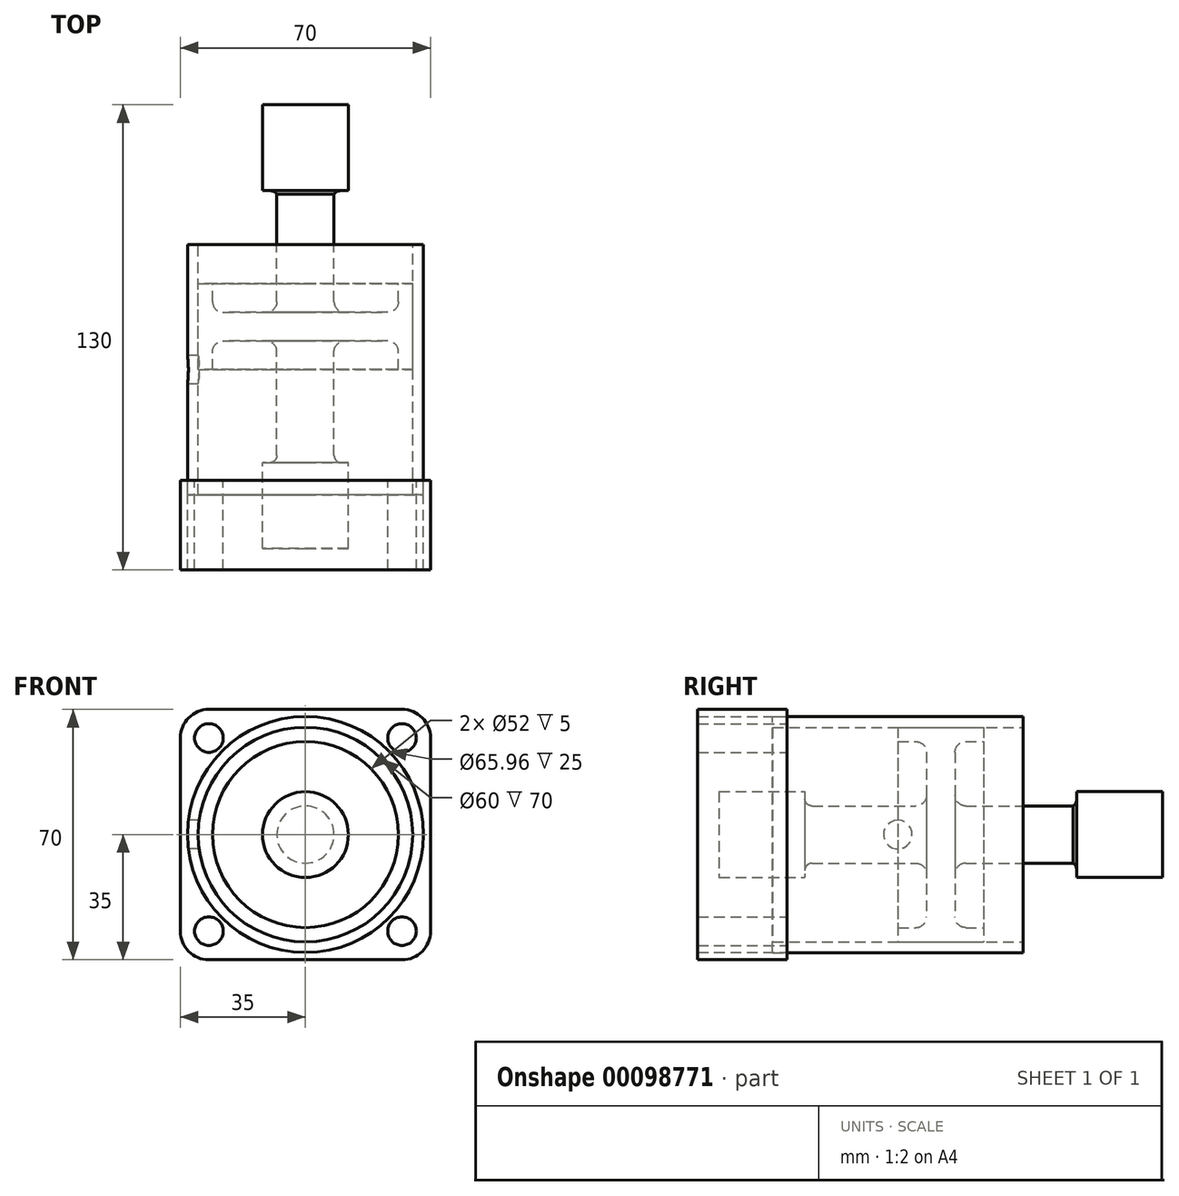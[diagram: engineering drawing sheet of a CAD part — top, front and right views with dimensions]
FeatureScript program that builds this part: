
annotation { "Feature Type Name" : "Feature", "Feature Type Description" : "" }
export const myFeature = defineFeature(function(context is Context, id is Id, definition is map)
    precondition{}
    {
        {
            var Q0;
            Q0=qCreatedBy(makeId("Right.planeOp"),FACE);
            var sketch = newSketch(context, id + "F0", { "sketchPlane" : qUnion([Q0])});
            skLineSegment(sketch, "E0", {"start": v(0, 26) * mm, "end": v(0, 30) * mm});
            skLineSegment(sketch, "E1", {"start": v(0, 30) * mm, "end": v(24, 30) * mm});
            skLineSegment(sketch, "E2", {"start": v(24, 30) * mm, "end": v(24, 26) * mm});
            skLineSegment(sketch, "E3", {"start": v(50, 9.73) * mm, "end": v(50, 12) * mm});
            skLineSegment(sketch, "E4", {"start": v(50, 12) * mm, "end": v(74, 12) * mm});
            skLineSegment(sketch, "E5", {"start": v(74, 12) * mm, "end": v(74, 0) * mm});
            skLineSegment(sketch, "E6", {"start": v(74, 0) * mm, "end": v(-50, 0) * mm});
            skLineSegment(sketch, "E7", {"start": v(-50, 0) * mm, "end": v(-50, 12) * mm});
            skLineSegment(sketch, "E8", {"start": v(-50, 12) * mm, "end": v(-26, 12) * mm});
            skLineSegment(sketch, "E9", {"start": v(-26, 12) * mm, "end": v(-26, 10) * mm});
            skPoint(sketch, "E10.visualSharp", {"position": v(-26, 8) * mm});
            skArc(sketch, "E10.filletArc", {"start": v(-26, 10) * mm, "mid": v(-25.41, 8.59) * mm, "end": v(-24, 8) * mm});
            skPoint(sketch, "E11.visualSharp", {"position": v(0, 8) * mm});
            skPoint(sketch, "E12.visualSharp", {"position": v(24, 8) * mm});
            skPoint(sketch, "E13.visualSharp", {"position": v(50, 8) * mm});
            skArc(sketch, "E13.filletArc", {"start": v(49, 8) * mm, "mid": v(49.73, 8.73) * mm, "end": v(50, 9.73) * mm});
            skLineSegment(sketch, "E14", {"start": v(-24, 8) * mm, "end": v(5, 8) * mm});
            skLineSegment(sketch, "E15", {"start": v(0, 26) * mm, "end": v(5, 26) * mm});
            skLineSegment(sketch, "E16", {"start": v(8, 23) * mm, "end": v(8, 11) * mm});
            skLineSegment(sketch, "E17", {"start": v(24, 26) * mm, "end": v(19, 26) * mm});
            skLineSegment(sketch, "E18", {"start": v(16, 23) * mm, "end": v(16, 11) * mm});
            skLineSegment(sketch, "E19.trimOffspring", {"start": v(19, 8) * mm, "end": v(49, 8) * mm});
            skPoint(sketch, "E20.visualSharp", {"position": v(8, 26) * mm});
            skArc(sketch, "E20.filletArc", {"start": v(8, 23) * mm, "mid": v(7.12, 25.12) * mm, "end": v(5, 26) * mm});
            skPoint(sketch, "E21.visualSharp", {"position": v(16, 26) * mm});
            skArc(sketch, "E21.filletArc", {"start": v(19, 26) * mm, "mid": v(16.88, 25.12) * mm, "end": v(16, 23) * mm});
            skPoint(sketch, "E22.visualSharp", {"position": v(8, 8) * mm});
            skArc(sketch, "E22.filletArc", {"start": v(5, 8) * mm, "mid": v(7.12, 8.88) * mm, "end": v(8, 11) * mm});
            skPoint(sketch, "E23.visualSharp", {"position": v(16, 8) * mm});
            skArc(sketch, "E23.filletArc", {"start": v(16, 11) * mm, "mid": v(16.88, 8.88) * mm, "end": v(19, 8) * mm});
            skSolve(sketch);
        }
        {
            var Q0;
            Q0=makeQuery(id+"F0.imprint","IMPRINT",FACE,{"disambiguationData":[TD([[makeQuery(id+"F0.imprint","IMPRINT",EDGE,{"derivedFrom":sQuery(id+"F0.wireOp",EDGE,"E0")}),-1.0]])]});
            var Q1;
            Q1=sQuery(id+"F0.wireOp",EDGE,"E6");
            revolve(context, id + "F1", {"surfaceOperationType" : NewSurfaceOperationType.NEW, "entities" : qUnion([Q0]), "axis" : qUnion([Q1]), "revolveType" : RevolveType.FULL});
        }
        {
            var Q0;
            Q0=makeQuery(id+"F1.opRevolve","SWEPT_FACE",FACE,{"disambiguationData":[OSD([sQuery(id+"F0.wireOp",EDGE,"E0")])]});
            var sketch = newSketch(context, id + "F2", { "sketchPlane" : qUnion([Q0])});
            skCircle(sketch, "E24", {"center": v(0, 0) * mm, "radius": 30 * mm});
            skCircle(sketch, "E25", {"center": v(0, 0) * mm, "radius": 33 * mm});
            skSolve(sketch);
        }
        {
            var Q0;
            Q0=makeQuery(id+"F2.imprint","IMPRINT",FACE,{"disambiguationData":[TD([[makeQuery(id+"F2.imprint","IMPRINT",EDGE,{"derivedFrom":sQuery(id+"F2.wireOp",EDGE,"E24")}),1.0]])]});
            extrude(context, id + "F3", {"entities" : qUnion([Q0]), "depth" : 70 * mm, "symmetric" : true});
        }
        {
            var Q0;
            Q0=qCreatedBy(makeId("Right.planeOp"),FACE);
            var sketch = newSketch(context, id + "F4", { "sketchPlane" : qUnion([Q0])});
            skPoint(sketch, "E26", {"position": v(0, 0) * mm});
            skSolve(sketch);
        }
        {
            var Q0;
            Q0=sQuery(id+"F4.wireOp",VERTEX,"E26");
            var Q1;
            Q1=makeQuery(id+"F3.opExtrude","SWEPT_BODY",BODY,{"disambiguationData":[OSD([sQuery(id+"F2.wireOp",EDGE,"E24"),sQuery(id+"F2.wireOp",EDGE,"E25")])]});
            hole(context, id + "F5", {"style" : HoleStyle.SIMPLE, "endStyle" : HoleEndStyle.BLIND, "holeDiameter" : 8 * mm, "holeDepth" : 70 * mm, "locations" : qUnion([Q0]), "scope" : qUnion([Q1])});
        }
        {
            var Q0;
            Q0=makeQuery(id+"F3.opExtrude","CAP_FACE",FACE,{"disambiguationData":[OSD([sQuery(id+"F2.wireOp",EDGE,"E24"),sQuery(id+"F2.wireOp",EDGE,"E25")])],"isStart":false});
            cPlane(context, id + "F6", {"entities" : qUnion([Q0]), "cplaneType" : CPlaneType.OFFSET, "offset" : 4 * mm, "oppositeDirection" : true, "width" : 150 * mm, "height" : 150 * mm});
        }
        {
            var Q0;
            Q0=qCreatedBy(id+"F6.planeOp",FACE);
            var sketch = newSketch(context, id + "F7", { "sketchPlane" : qUnion([Q0])});
            skLineSegment(sketch, "E27.bottom", {"start": v(27, 35) * mm, "end": v(-27, 35) * mm});
            skLineSegment(sketch, "E27.top", {"start": v(27, -35) * mm, "end": v(-27, -35) * mm});
            skLineSegment(sketch, "E27.left", {"start": v(35, 27) * mm, "end": v(35, -27) * mm});
            skLineSegment(sketch, "E27.right", {"start": v(-35, 27) * mm, "end": v(-35, -27) * mm});
            skPoint(sketch, "E27.middle", {"position": v(0, 0) * mm});
            skPoint(sketch, "E28.visualSharp", {"position": v(-35, 35) * mm});
            skArc(sketch, "E28.filletArc", {"start": v(-27, 35) * mm, "mid": v(-32.66, 32.66) * mm, "end": v(-35, 27) * mm});
            skPoint(sketch, "E29.visualSharp", {"position": v(35, 35) * mm});
            skArc(sketch, "E29.filletArc", {"start": v(35, 27) * mm, "mid": v(32.66, 32.66) * mm, "end": v(27, 35) * mm});
            skPoint(sketch, "E30.visualSharp", {"position": v(35, -35) * mm});
            skArc(sketch, "E30.filletArc", {"start": v(27, -35) * mm, "mid": v(32.66, -32.66) * mm, "end": v(35, -27) * mm});
            skPoint(sketch, "E31.visualSharp", {"position": v(-35, -35) * mm});
            skArc(sketch, "E31.filletArc", {"start": v(-35, -27) * mm, "mid": v(-32.66, -32.66) * mm, "end": v(-27, -35) * mm});
            skCircle(sketch, "E32", {"center": v(-27, 27) * mm, "radius": 4 * mm});
            skCircle(sketch, "E33", {"center": v(27, 27) * mm, "radius": 4 * mm});
            skCircle(sketch, "E34", {"center": v(27, -27) * mm, "radius": 4 * mm});
            skCircle(sketch, "E35", {"center": v(-27, -27) * mm, "radius": 4 * mm});
            skCircle(sketch, "E36", {"center": v(0, 0) * mm, "radius": 32.98 * mm});
            skSolve(sketch);
        }
        {
            var Q0;
            Q0=makeQuery(id+"F7.imprint","IMPRINT",FACE,{"disambiguationData":[TD([[makeQuery(id+"F7.imprint","IMPRINT",EDGE,{"derivedFrom":sQuery(id+"F7.wireOp",EDGE,"E27.bottom")}),1.0]])]});
            extrude(context, id + "F8", {"entities" : qUnion([Q0]), "offsetDistance" : 25 * mm, "depth" : 25 * mm});
        }
    });
